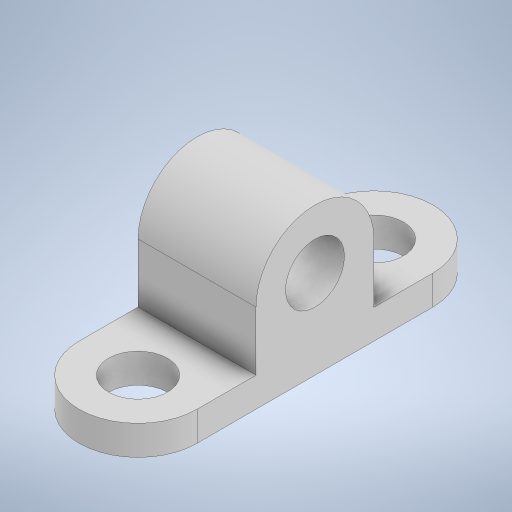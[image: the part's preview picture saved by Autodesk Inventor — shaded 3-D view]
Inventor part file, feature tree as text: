
AUTODESK INVENTOR PART (.ipt)
format: ipt  version: 2023 (Build 270158000, 158)  size: 256,000 bytes
history: native  units: in
note: dims shown in document units (in); Inventor stores cm internally (conversion verified against a paired STEP export)
features: sketch x3, extrude x2
ambient origin geometry x8: Origin, YZ Plane, XZ Plane, XY Plane, X Axis, Y Axis, Z Axis, Center Point
bodies: Solid1 (feature_tree)
feature tree (5):
  sketch  "Sketch1"  dims[d3=0.7874in d4=1.5748in]
  extrude  "Extrusion1"  Depth=1.5748in
  extrude  "Extrusion2"  Depth=1.5748in
  sketch  "Sketch2"  dims[d6=0.7874in d7=1.5748in]
  sketch  "Sketch3"  dims[d8=1.5748in d9=1.5748in d10=0.3937in d11=0.0in d13=1.5748in d14=0.7874in d15=1.5748in d16=0.0in]
